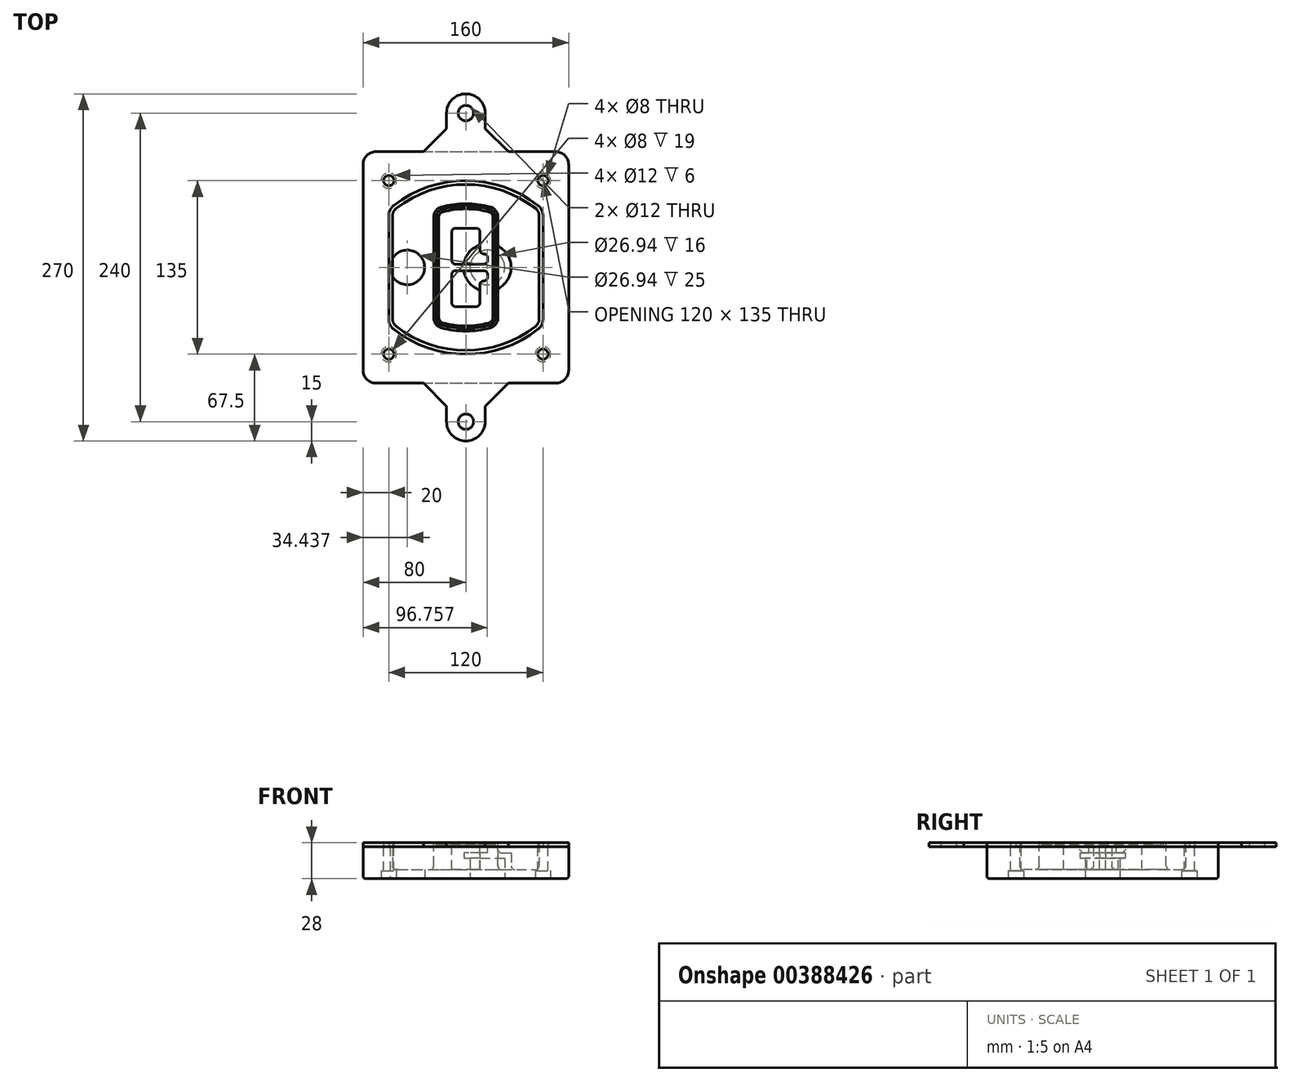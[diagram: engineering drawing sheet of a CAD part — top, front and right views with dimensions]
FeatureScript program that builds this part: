
annotation { "Feature Type Name" : "Feature", "Feature Type Description" : "" }
export const myFeature = defineFeature(function(context is Context, id is Id, definition is map)
    precondition{}
    {
        {
            var Q0;
            Q0=qCreatedBy(makeId("Top.planeOp"),FACE);
            var sketch = newSketch(context, id + "F0", { "sketchPlane" : qUnion([Q0])});
            skPoint(sketch, "E0.rect.middle", {"position": v(0, 0) * mm});
            skLineSegment(sketch, "E1.bottom", {"start": v(-70, -90) * mm, "end": v(70, -90) * mm});
            skLineSegment(sketch, "E1.top", {"start": v(-70, 90) * mm, "end": v(70, 90) * mm});
            skLineSegment(sketch, "E1.left", {"start": v(-80, -80) * mm, "end": v(-80, 80) * mm});
            skLineSegment(sketch, "E1.right", {"start": v(80, -80) * mm, "end": v(80, 80) * mm});
            skLineSegment(sketch, "E2", {"start": v(-80, 90) * mm, "end": v(80, -90) * mm, "construction": true});
            skLineSegment(sketch, "E3", {"start": v(80, 90) * mm, "end": v(-80, -90) * mm, "construction": true});
            skCircle(sketch, "E4", {"center": v(-60, 67.5) * mm, "radius": 4 * mm});
            skCircle(sketch, "E5", {"center": v(60, 67.5) * mm, "radius": 4 * mm});
            skCircle(sketch, "E6", {"center": v(60, -67.5) * mm, "radius": 4 * mm});
            skCircle(sketch, "E7", {"center": v(-60, -67.5) * mm, "radius": 4 * mm});
            skLineSegment(sketch, "E8", {"start": v(-60, 67.5) * mm, "end": v(60, 67.5) * mm, "construction": true});
            skLineSegment(sketch, "E9", {"start": v(60, 67.5) * mm, "end": v(60, -67.5) * mm, "construction": true});
            skLineSegment(sketch, "E10", {"start": v(60, -67.5) * mm, "end": v(-60, -67.5) * mm, "construction": true});
            skLineSegment(sketch, "E11", {"start": v(-60, -67.5) * mm, "end": v(-60, 67.5) * mm, "construction": true});
            skLineSegment(sketch, "E12", {"start": v(-60, 40.3) * mm, "end": v(-60, -40.3) * mm});
            skLineSegment(sketch, "E13", {"start": v(60, 40.3) * mm, "end": v(60, -40.3) * mm});
            skArc(sketch, "E14", {"start": v(56.15, 48.18) * mm, "mid": v(0, 67.5) * mm, "end": v(-56.15, 48.18) * mm});
            skArc(sketch, "E15", {"start": v(-56.15, -48.18) * mm, "mid": v(0, -67.5) * mm, "end": v(56.15, -48.18) * mm});
            skLineSegment(sketch, "E16", {"start": v(-60, 0) * mm, "end": v(60, 0) * mm, "construction": true});
            skPoint(sketch, "E17.visualSharp", {"position": v(-60, -45) * mm});
            skArc(sketch, "E17.filletArc", {"start": v(-60, -40.3) * mm, "mid": v(-58.99, -44.68) * mm, "end": v(-56.15, -48.18) * mm});
            skPoint(sketch, "E18.visualSharp", {"position": v(-60, 45) * mm});
            skArc(sketch, "E18.filletArc", {"start": v(-56.15, 48.18) * mm, "mid": v(-58.99, 44.68) * mm, "end": v(-60, 40.3) * mm});
            skPoint(sketch, "E19.visualSharp", {"position": v(60, 45) * mm});
            skArc(sketch, "E19.filletArc", {"start": v(60, 40.3) * mm, "mid": v(58.99, 44.68) * mm, "end": v(56.15, 48.18) * mm});
            skPoint(sketch, "E20.visualSharp", {"position": v(60, -45) * mm});
            skArc(sketch, "E20.filletArc", {"start": v(56.15, -48.18) * mm, "mid": v(58.99, -44.68) * mm, "end": v(60, -40.3) * mm});
            skPoint(sketch, "E21.visualSharp", {"position": v(-80, 90) * mm});
            skArc(sketch, "E21.filletArc", {"start": v(-70, 90) * mm, "mid": v(-77.07, 87.07) * mm, "end": v(-80, 80) * mm});
            skPoint(sketch, "E22.visualSharp", {"position": v(80, 90) * mm});
            skArc(sketch, "E22.filletArc", {"start": v(80, 80) * mm, "mid": v(77.07, 87.07) * mm, "end": v(70, 90) * mm});
            skPoint(sketch, "E23.visualSharp", {"position": v(80, -90) * mm});
            skArc(sketch, "E23.filletArc", {"start": v(70, -90) * mm, "mid": v(77.07, -87.07) * mm, "end": v(80, -80) * mm});
            skPoint(sketch, "E24.visualSharp", {"position": v(-80, -90) * mm});
            skArc(sketch, "E24.filletArc", {"start": v(-80, -80) * mm, "mid": v(-77.07, -87.07) * mm, "end": v(-70, -90) * mm});
            skArc(sketch, "E25.0", {"start": v(57, 40.3) * mm, "mid": v(56.3, 43.36) * mm, "end": v(54.3, 45.81) * mm});
            skLineSegment(sketch, "E25.1", {"start": v(57, 40.3) * mm, "end": v(57, -40.3) * mm});
            skArc(sketch, "E25.2", {"start": v(54.3, -45.81) * mm, "mid": v(56.3, -43.36) * mm, "end": v(57, -40.3) * mm});
            skArc(sketch, "E25.3", {"start": v(-54.3, -45.81) * mm, "mid": v(0, -64.5) * mm, "end": v(54.3, -45.81) * mm});
            skArc(sketch, "E25.4", {"start": v(-57, -40.3) * mm, "mid": v(-56.3, -43.36) * mm, "end": v(-54.3, -45.81) * mm});
            skArc(sketch, "E25.5", {"start": v(54.3, 45.81) * mm, "mid": v(0, 64.5) * mm, "end": v(-54.3, 45.81) * mm});
            skLineSegment(sketch, "E25.6", {"start": v(-57, 40.3) * mm, "end": v(-57, -40.3) * mm});
            skArc(sketch, "E25.7", {"start": v(-54.3, 45.81) * mm, "mid": v(-56.3, 43.36) * mm, "end": v(-57, 40.3) * mm});
            skArc(sketch, "E26.0", {"start": v(-58.62, 51.33) * mm, "mid": v(-62.58, 46.43) * mm, "end": v(-64, 40.3) * mm});
            skArc(sketch, "E26.1", {"start": v(58.62, 51.33) * mm, "mid": v(0, 71.5) * mm, "end": v(-58.62, 51.33) * mm});
            skArc(sketch, "E26.2", {"start": v(64, 40.3) * mm, "mid": v(62.58, 46.43) * mm, "end": v(58.62, 51.33) * mm});
            skLineSegment(sketch, "E26.3", {"start": v(64, 40.3) * mm, "end": v(64, -40.3) * mm});
            skArc(sketch, "E26.4", {"start": v(58.62, -51.33) * mm, "mid": v(62.58, -46.43) * mm, "end": v(64, -40.3) * mm});
            skLineSegment(sketch, "E26.5", {"start": v(-64, 40.3) * mm, "end": v(-64, -40.3) * mm});
            skArc(sketch, "E26.6", {"start": v(-58.62, -51.33) * mm, "mid": v(0, -71.5) * mm, "end": v(58.62, -51.33) * mm});
            skArc(sketch, "E26.7", {"start": v(-64, -40.3) * mm, "mid": v(-62.58, -46.43) * mm, "end": v(-58.62, -51.33) * mm});
            skSolve(sketch);
        }
        {
            var Q0;
            Q0=makeQuery(id+"F0.imprint","IMPRINT",FACE,{"disambiguationData":[TD([[makeQuery(id+"F0.imprint","IMPRINT",EDGE,{"derivedFrom":sQuery(id+"F0.wireOp",EDGE,"E1.bottom")}),1.0]])]});
            var Q1;
            Q1=makeQuery(id+"F0.imprint","IMPRINT",FACE,{"disambiguationData":[TD([[makeQuery(id+"F0.imprint","IMPRINT",EDGE,{"derivedFrom":sQuery(id+"F0.wireOp",EDGE,"E12")}),1.0]])]});
            var Q2;
            Q2=makeQuery(id+"F0.imprint","IMPRINT",FACE,{"disambiguationData":[TD([[makeQuery(id+"F0.imprint","IMPRINT",EDGE,{"derivedFrom":sQuery(id+"F0.wireOp",EDGE,"E25.0")}),1.0]])]});
            var Q3;
            Q3=makeQuery(id+"F0.imprint","IMPRINT",FACE,{"disambiguationData":[TD([[makeQuery(id+"F0.imprint","IMPRINT",EDGE,{"derivedFrom":sQuery(id+"F0.wireOp",EDGE,"E12")}),-1.0]])]});
            extrude(context, id + "F1", {"entities" : qUnion([Q0, Q1, Q2, Q3]), "oppositeDirection" : true, "depth" : 25 * mm});
        }
        {
            var Q0;
            Q0=makeQuery(id+"F0.imprint","IMPRINT",FACE,{"disambiguationData":[TD([[makeQuery(id+"F0.imprint","IMPRINT",EDGE,{"derivedFrom":sQuery(id+"F0.wireOp",EDGE,"E12")}),1.0]])]});
            extrude(context, id + "F2", {"entities" : qUnion([Q0]), "operationType" : NewBodyOperationType.ADD, "depth" : 3 * mm});
        }
        {
            var Q0;
            Q0=makeQuery(id+"F0.imprint","IMPRINT",FACE,{"disambiguationData":[TD([[makeQuery(id+"F0.imprint","IMPRINT",EDGE,{"derivedFrom":sQuery(id+"F0.wireOp",EDGE,"E25.0")}),1.0]])]});
            extrude(context, id + "F3", {"entities" : qUnion([Q0]), "operationType" : NewBodyOperationType.REMOVE, "oppositeDirection" : true, "depth" : 18 * mm});
        }
        {
            var Q0;
            Q0=makeQuery(id+"F2.opExtrude","CAP_FACE",FACE,{"disambiguationData":[OSD([sQuery(id+"F0.wireOp",EDGE,"E12"),sQuery(id+"F0.wireOp",EDGE,"E13"),sQuery(id+"F0.wireOp",EDGE,"E14"),sQuery(id+"F0.wireOp",EDGE,"E15"),sQuery(id+"F0.wireOp",EDGE,"E17.filletArc"),sQuery(id+"F0.wireOp",EDGE,"E18.filletArc"),sQuery(id+"F0.wireOp",EDGE,"E19.filletArc"),sQuery(id+"F0.wireOp",EDGE,"E20.filletArc"),sQuery(id+"F0.wireOp",EDGE,"E25.0"),sQuery(id+"F0.wireOp",EDGE,"E25.1"),sQuery(id+"F0.wireOp",EDGE,"E25.2"),sQuery(id+"F0.wireOp",EDGE,"E25.3"),sQuery(id+"F0.wireOp",EDGE,"E25.4"),sQuery(id+"F0.wireOp",EDGE,"E25.5"),sQuery(id+"F0.wireOp",EDGE,"E25.6"),sQuery(id+"F0.wireOp",EDGE,"E25.7")])],"isStart":false});
            var sketch = newSketch(context, id + "F4", { "sketchPlane" : qUnion([Q0])});
            skArc(sketch, "E27.0", {"start": v(-19.08, -46.97) * mm, "mid": v(0, -49.5) * mm, "end": v(19.08, -46.97) * mm});
            skArc(sketch, "E28.0", {"start": v(19.08, 46.97) * mm, "mid": v(0, 49.5) * mm, "end": v(-19.08, 46.97) * mm});
            skLineSegment(sketch, "E29", {"start": v(-25, 39.25) * mm, "end": v(-25, -39.25) * mm});
            skLineSegment(sketch, "E30", {"start": v(25, 39.25) * mm, "end": v(25, -39.25) * mm});
            skLineSegment(sketch, "E31", {"start": v(-25, 45.1) * mm, "end": v(25, 45.1) * mm, "construction": true});
            skLineSegment(sketch, "E32", {"start": v(-25, -45.1) * mm, "end": v(25, -45.1) * mm, "construction": true});
            skPoint(sketch, "E33.visualSharp", {"position": v(-25, 45.1) * mm});
            skArc(sketch, "E33.filletArc", {"start": v(-19.08, 46.97) * mm, "mid": v(-23.35, 44.11) * mm, "end": v(-25, 39.25) * mm});
            skPoint(sketch, "E34.visualSharp", {"position": v(25, 45.1) * mm});
            skArc(sketch, "E34.filletArc", {"start": v(25, 39.25) * mm, "mid": v(23.35, 44.11) * mm, "end": v(19.08, 46.97) * mm});
            skPoint(sketch, "E35.visualSharp", {"position": v(25, -45.1) * mm});
            skArc(sketch, "E35.filletArc", {"start": v(19.08, -46.97) * mm, "mid": v(23.35, -44.11) * mm, "end": v(25, -39.25) * mm});
            skPoint(sketch, "E36.visualSharp", {"position": v(-25, -45.1) * mm});
            skArc(sketch, "E36.filletArc", {"start": v(-25, -39.25) * mm, "mid": v(-23.35, -44.11) * mm, "end": v(-19.08, -46.97) * mm});
            skArc(sketch, "E37.0", {"start": v(54.3, 45.81) * mm, "mid": v(0, 64.5) * mm, "end": v(-54.3, 45.81) * mm});
            skArc(sketch, "E37.1", {"start": v(-54.3, 45.81) * mm, "mid": v(-56.3, 43.36) * mm, "end": v(-57, 40.3) * mm});
            skLineSegment(sketch, "E37.2", {"start": v(-57, 40.3) * mm, "end": v(-57, -40.3) * mm});
            skArc(sketch, "E37.3", {"start": v(-57, -40.3) * mm, "mid": v(-56.3, -43.36) * mm, "end": v(-54.3, -45.81) * mm});
            skArc(sketch, "E37.4", {"start": v(-54.3, -45.81) * mm, "mid": v(0, -64.5) * mm, "end": v(54.3, -45.81) * mm});
            skArc(sketch, "E37.5", {"start": v(54.3, -45.81) * mm, "mid": v(56.3, -43.36) * mm, "end": v(57, -40.3) * mm});
            skLineSegment(sketch, "E37.6", {"start": v(57, 40.3) * mm, "end": v(57, -40.3) * mm});
            skArc(sketch, "E37.7", {"start": v(57, 40.3) * mm, "mid": v(56.3, 43.36) * mm, "end": v(54.3, 45.81) * mm});
            skLineSegment(sketch, "E38.0", {"start": v(23, 39.25) * mm, "end": v(23, -39.25) * mm});
            skArc(sketch, "E38.1", {"start": v(18.56, -45.04) * mm, "mid": v(21.76, -42.9) * mm, "end": v(23, -39.25) * mm});
            skArc(sketch, "E38.2", {"start": v(-18.56, -45.04) * mm, "mid": v(0, -47.5) * mm, "end": v(18.56, -45.04) * mm});
            skArc(sketch, "E38.3", {"start": v(-23, -39.25) * mm, "mid": v(-21.76, -42.9) * mm, "end": v(-18.56, -45.04) * mm});
            skLineSegment(sketch, "E38.4", {"start": v(-23, 39.25) * mm, "end": v(-23, -39.25) * mm});
            skArc(sketch, "E38.5", {"start": v(23, 39.25) * mm, "mid": v(21.76, 42.9) * mm, "end": v(18.56, 45.04) * mm});
            skArc(sketch, "E38.6", {"start": v(-18.56, 45.04) * mm, "mid": v(-21.76, 42.9) * mm, "end": v(-23, 39.25) * mm});
            skArc(sketch, "E38.7", {"start": v(18.56, 45.04) * mm, "mid": v(0, 47.5) * mm, "end": v(-18.56, 45.04) * mm});
            skArc(sketch, "E39.0", {"start": v(21, 39.25) * mm, "mid": v(20.18, 41.68) * mm, "end": v(18.04, 43.1) * mm});
            skLineSegment(sketch, "E39.1", {"start": v(21, 39.25) * mm, "end": v(21, -39.25) * mm});
            skArc(sketch, "E39.2", {"start": v(18.04, -43.1) * mm, "mid": v(20.18, -41.68) * mm, "end": v(21, -39.25) * mm});
            skArc(sketch, "E39.3", {"start": v(-18.04, -43.1) * mm, "mid": v(0, -45.5) * mm, "end": v(18.04, -43.1) * mm});
            skArc(sketch, "E39.4", {"start": v(-21, -39.25) * mm, "mid": v(-20.18, -41.68) * mm, "end": v(-18.04, -43.1) * mm});
            skArc(sketch, "E39.5", {"start": v(18.04, 43.1) * mm, "mid": v(0, 45.5) * mm, "end": v(-18.04, 43.1) * mm});
            skLineSegment(sketch, "E39.6", {"start": v(-21, 39.25) * mm, "end": v(-21, -39.25) * mm});
            skArc(sketch, "E39.7", {"start": v(-18.04, 43.1) * mm, "mid": v(-20.18, 41.68) * mm, "end": v(-21, 39.25) * mm});
            skLineSegment(sketch, "E40", {"start": v(-25, 0) * mm, "end": v(25, 0) * mm, "construction": true});
            skLineSegment(sketch, "E41", {"start": v(-11, 5.5) * mm, "end": v(-11, 27.5) * mm});
            skLineSegment(sketch, "E42", {"start": v(-8, 30.5) * mm, "end": v(8, 30.5) * mm});
            skLineSegment(sketch, "E43", {"start": v(11, 27.5) * mm, "end": v(11, 13.5) * mm});
            skLineSegment(sketch, "E44", {"start": v(14, 10.5) * mm, "end": v(14, 10.5) * mm});
            skLineSegment(sketch, "E45", {"start": v(17, 7.5) * mm, "end": v(17, 5.5) * mm});
            skLineSegment(sketch, "E46", {"start": v(14, 2.5) * mm, "end": v(-8, 2.5) * mm});
            skPoint(sketch, "E47.visualSharp", {"position": v(-11, 30.5) * mm});
            skArc(sketch, "E47.filletArc", {"start": v(-8, 30.5) * mm, "mid": v(-10.12, 29.62) * mm, "end": v(-11, 27.5) * mm});
            skPoint(sketch, "E48.visualSharp", {"position": v(11, 30.5) * mm});
            skArc(sketch, "E48.filletArc", {"start": v(11, 27.5) * mm, "mid": v(10.12, 29.62) * mm, "end": v(8, 30.5) * mm});
            skPoint(sketch, "E49.visualSharp", {"position": v(11, 10.5) * mm});
            skArc(sketch, "E49.filletArc", {"start": v(11, 13.5) * mm, "mid": v(11.88, 11.38) * mm, "end": v(14, 10.5) * mm});
            skPoint(sketch, "E50.visualSharp", {"position": v(17, 10.5) * mm});
            skArc(sketch, "E50.filletArc", {"start": v(17, 7.5) * mm, "mid": v(16.12, 9.62) * mm, "end": v(14, 10.5) * mm});
            skPoint(sketch, "E51.visualSharp", {"position": v(17, 2.5) * mm});
            skArc(sketch, "E51.filletArc", {"start": v(14, 2.5) * mm, "mid": v(16.12, 3.38) * mm, "end": v(17, 5.5) * mm});
            skPoint(sketch, "E52.visualSharp", {"position": v(-11, 2.5) * mm});
            skArc(sketch, "E52.filletArc", {"start": v(-11, 5.5) * mm, "mid": v(-10.12, 3.38) * mm, "end": v(-8, 2.5) * mm});
            skLineSegment(sketch, "E53.0.MirrorCS", {"start": v(14, -2.5) * mm, "end": v(-8, -2.5) * mm});
            skArc(sketch, "E54.0.MirrorCS", {"start": v(-11, -5.5) * mm, "mid": v(-10.12, -3.38) * mm, "end": v(-8, -2.5) * mm});
            skLineSegment(sketch, "E55.0.MirrorCS", {"start": v(-11, -5.5) * mm, "end": v(-11, -27.5) * mm});
            skArc(sketch, "E56.0.MirrorCS", {"start": v(-8, -30.5) * mm, "mid": v(-10.12, -29.62) * mm, "end": v(-11, -27.5) * mm});
            skLineSegment(sketch, "E57.0.MirrorCS", {"start": v(-8, -30.5) * mm, "end": v(8, -30.5) * mm});
            skArc(sketch, "E58.0.MirrorCS", {"start": v(11, -27.5) * mm, "mid": v(10.12, -29.62) * mm, "end": v(8, -30.5) * mm});
            skLineSegment(sketch, "E59.0.MirrorCS", {"start": v(11, -27.5) * mm, "end": v(11, -13.5) * mm});
            skArc(sketch, "E60.0.MirrorCS", {"start": v(11, -13.5) * mm, "mid": v(11.88, -11.38) * mm, "end": v(14, -10.5) * mm});
            skArc(sketch, "E61.0.MirrorCS", {"start": v(17, -7.5) * mm, "mid": v(16.12, -9.62) * mm, "end": v(14, -10.5) * mm});
            skLineSegment(sketch, "E62.0.MirrorCS", {"start": v(17, -7.5) * mm, "end": v(17, -5.5) * mm});
            skArc(sketch, "E63.0.MirrorCS", {"start": v(14, -2.5) * mm, "mid": v(16.12, -3.38) * mm, "end": v(17, -5.5) * mm});
            skSolve(sketch);
        }
        {
            var Q0;
            Q0=makeQuery(id+"F4.imprint","IMPRINT",FACE,{"disambiguationData":[TD([[makeQuery(id+"F4.imprint","IMPRINT",EDGE,{"derivedFrom":sQuery(id+"F4.wireOp",EDGE,"E27.0")}),1.0]])]});
            var Q1;
            Q1=makeQuery(id+"F4.imprint","IMPRINT",FACE,{"disambiguationData":[TD([[makeQuery(id+"F4.imprint","IMPRINT",EDGE,{"derivedFrom":sQuery(id+"F4.wireOp",EDGE,"E38.0")}),-1.0]])]});
            var Q2;
            Q2=makeQuery(id+"F4.imprint","IMPRINT",FACE,{"disambiguationData":[TD([[makeQuery(id+"F4.imprint","IMPRINT",EDGE,{"derivedFrom":sQuery(id+"F4.wireOp",EDGE,"E39.0")}),1.0]])]});
            extrude(context, id + "F5", {"entities" : qUnion([Q0, Q1, Q2]), "operationType" : NewBodyOperationType.ADD, "endBound" : BoundingType.UP_TO_NEXT, "oppositeDirection" : true, "depth" : 25 * mm});
        }
        {
            var Q0;
            Q0=makeQuery(id+"F4.imprint","IMPRINT",FACE,{"disambiguationData":[TD([[makeQuery(id+"F4.imprint","IMPRINT",EDGE,{"derivedFrom":sQuery(id+"F4.wireOp",EDGE,"E38.0")}),-1.0]])]});
            extrude(context, id + "F6", {"entities" : qUnion([Q0]), "operationType" : NewBodyOperationType.REMOVE, "oppositeDirection" : true, "depth" : 2 * mm});
        }
        {
            var Q0;
            Q0=makeQuery(id+"F1.opExtrude","CAP_FACE",FACE,{"disambiguationData":[OSD([sQuery(id+"F0.wireOp",EDGE,"E1.bottom"),sQuery(id+"F0.wireOp",EDGE,"E1.top"),sQuery(id+"F0.wireOp",EDGE,"E1.left"),sQuery(id+"F0.wireOp",EDGE,"E1.right"),sQuery(id+"F0.wireOp",EDGE,"E4"),sQuery(id+"F0.wireOp",EDGE,"E5"),sQuery(id+"F0.wireOp",EDGE,"E6"),sQuery(id+"F0.wireOp",EDGE,"E7"),sQuery(id+"F0.wireOp",EDGE,"E21.filletArc"),sQuery(id+"F0.wireOp",EDGE,"E22.filletArc"),sQuery(id+"F0.wireOp",EDGE,"E23.filletArc"),sQuery(id+"F0.wireOp",EDGE,"E24.filletArc")])],"isStart":false});
            var sketch = newSketch(context, id + "F7", { "sketchPlane" : qUnion([Q0])});
            skCircle(sketch, "E64", {"center": v(16.76, 0) * mm, "radius": 13.47 * mm});
            skCircle(sketch, "E65", {"center": v(-45.56, 0) * mm, "radius": 13.47 * mm});
            skLineSegment(sketch, "E66", {"start": v(80, 0) * mm, "end": v(-80, 0) * mm});
            skCircle(sketch, "E67", {"center": v(16.76, 0) * mm, "radius": 18.47 * mm});
            skCircle(sketch, "E68", {"center": v(60, -67.5) * mm, "radius": 6 * mm});
            skCircle(sketch, "E69", {"center": v(-60, -67.5) * mm, "radius": 6 * mm});
            skCircle(sketch, "E70", {"center": v(-60, 67.5) * mm, "radius": 6 * mm});
            skCircle(sketch, "E71", {"center": v(60, 67.5) * mm, "radius": 6 * mm});
            skSolve(sketch);
        }
        {
            var Q0;
            {var subQ1=sQuery(id+"F7.wireOp",EDGE,"E66");var subQ4=sQuery(id+"F7.wireOp",EDGE,"E64");var subQ6=makeQuery(id+"F7.imprint","INTERSECT",VERTEX,{"disambiguationData":[OD(0.0)],"derivedFrom":[subQ4,subQ1]});Q0=makeQuery(id+"F7.imprint","IMPRINT",FACE,{"disambiguationData":[TD([[makeQuery(id+"F7.imprint","IMPRINT",EDGE,{"disambiguationData":[TD([[subQ6,-1.0]])],"derivedFrom":subQ4}),-1.0]])]});}
            var Q1;
            {var subQ0=sQuery(id+"F7.wireOp",EDGE,"E66");var subQ1=sQuery(id+"F7.wireOp",EDGE,"E64");var subQ3=makeQuery(id+"F7.imprint","INTERSECT",VERTEX,{"disambiguationData":[OD(0.0)],"derivedFrom":[subQ1,subQ0]});Q1=makeQuery(id+"F7.imprint","IMPRINT",FACE,{"disambiguationData":[TD([[makeQuery(id+"F7.imprint","IMPRINT",EDGE,{"disambiguationData":[TD([[subQ3,-1.0]])],"derivedFrom":subQ1}),1.0]])]});}
            var Q2;
            {var subQ0=sQuery(id+"F7.wireOp",EDGE,"E66");var subQ1=sQuery(id+"F7.wireOp",EDGE,"E64");var subQ3=makeQuery(id+"F7.imprint","INTERSECT",VERTEX,{"disambiguationData":[OD(0.0)],"derivedFrom":[subQ1,subQ0]});Q2=makeQuery(id+"F7.imprint","IMPRINT",FACE,{"disambiguationData":[TD([[makeQuery(id+"F7.imprint","IMPRINT",EDGE,{"disambiguationData":[TD([[subQ3,1.0]])],"derivedFrom":subQ1}),1.0]])]});}
            var Q3;
            {var subQ1=sQuery(id+"F7.wireOp",EDGE,"E66");var subQ4=sQuery(id+"F7.wireOp",EDGE,"E64");var subQ6=makeQuery(id+"F7.imprint","INTERSECT",VERTEX,{"disambiguationData":[OD(0.0)],"derivedFrom":[subQ4,subQ1]});Q3=makeQuery(id+"F7.imprint","IMPRINT",FACE,{"disambiguationData":[TD([[makeQuery(id+"F7.imprint","IMPRINT",EDGE,{"disambiguationData":[TD([[subQ6,1.0]])],"derivedFrom":subQ4}),-1.0]])]});}
            extrude(context, id + "F8", {"entities" : qUnion([Q0, Q1, Q2, Q3]), "operationType" : NewBodyOperationType.ADD, "oppositeDirection" : true, "depth" : 20 * mm});
        }
        {
            var Q0;
            {var subQ0=sQuery(id+"F7.wireOp",EDGE,"E66");var subQ1=sQuery(id+"F7.wireOp",EDGE,"E64");var subQ3=makeQuery(id+"F7.imprint","INTERSECT",VERTEX,{"disambiguationData":[OD(0.0)],"derivedFrom":[subQ1,subQ0]});Q0=makeQuery(id+"F7.imprint","IMPRINT",FACE,{"disambiguationData":[TD([[makeQuery(id+"F7.imprint","IMPRINT",EDGE,{"disambiguationData":[TD([[subQ3,-1.0]])],"derivedFrom":subQ1}),1.0]])]});}
            var Q1;
            {var subQ0=sQuery(id+"F7.wireOp",EDGE,"E66");var subQ1=sQuery(id+"F7.wireOp",EDGE,"E64");var subQ3=makeQuery(id+"F7.imprint","INTERSECT",VERTEX,{"disambiguationData":[OD(0.0)],"derivedFrom":[subQ1,subQ0]});Q1=makeQuery(id+"F7.imprint","IMPRINT",FACE,{"disambiguationData":[TD([[makeQuery(id+"F7.imprint","IMPRINT",EDGE,{"disambiguationData":[TD([[subQ3,1.0]])],"derivedFrom":subQ1}),1.0]])]});}
            extrude(context, id + "F9", {"entities" : qUnion([Q0, Q1]), "operationType" : NewBodyOperationType.REMOVE, "oppositeDirection" : true, "depth" : 16 * mm});
        }
        {
            var Q0;
            {var subQ0=sQuery(id+"F7.wireOp",EDGE,"E66");var subQ1=sQuery(id+"F7.wireOp",EDGE,"E65");var subQ3=makeQuery(id+"F7.imprint","INTERSECT",VERTEX,{"disambiguationData":[OD(0.0)],"derivedFrom":[subQ1,subQ0]});Q0=makeQuery(id+"F7.imprint","IMPRINT",FACE,{"disambiguationData":[TD([[makeQuery(id+"F7.imprint","IMPRINT",EDGE,{"disambiguationData":[TD([[subQ3,-1.0]])],"derivedFrom":subQ1}),1.0]])]});}
            var Q1;
            {var subQ0=sQuery(id+"F7.wireOp",EDGE,"E66");var subQ1=sQuery(id+"F7.wireOp",EDGE,"E65");var subQ3=makeQuery(id+"F7.imprint","INTERSECT",VERTEX,{"disambiguationData":[OD(0.0)],"derivedFrom":[subQ1,subQ0]});Q1=makeQuery(id+"F7.imprint","IMPRINT",FACE,{"disambiguationData":[TD([[makeQuery(id+"F7.imprint","IMPRINT",EDGE,{"disambiguationData":[TD([[subQ3,1.0]])],"derivedFrom":subQ1}),1.0]])]});}
            extrude(context, id + "F10", {"entities" : qUnion([Q0, Q1]), "operationType" : NewBodyOperationType.REMOVE, "oppositeDirection" : true, "depth" : 25 * mm});
        }
        {
            var Q0;
            Q0=makeQuery(id+"F7.imprint","IMPRINT",FACE,{"disambiguationData":[TD([[makeQuery(id+"F7.imprint","IMPRINT",EDGE,{"derivedFrom":sQuery(id+"F7.wireOp",EDGE,"E68")}),1.0]])]});
            var Q1;
            Q1=makeQuery(id+"F7.imprint","IMPRINT",FACE,{"disambiguationData":[TD([[makeQuery(id+"F7.imprint","IMPRINT",EDGE,{"derivedFrom":makeQuery(id+"F1.opExtrude","CAP_EDGE",EDGE,{"disambiguationData":[OSD([sQuery(id+"F0.wireOp",EDGE,"E5")])],"isStart":false})}),-1.0]])]});
            var Q2;
            Q2=makeQuery(id+"F7.imprint","IMPRINT",FACE,{"disambiguationData":[TD([[makeQuery(id+"F7.imprint","IMPRINT",EDGE,{"derivedFrom":sQuery(id+"F7.wireOp",EDGE,"E69")}),1.0]])]});
            var Q3;
            Q3=makeQuery(id+"F7.imprint","IMPRINT",FACE,{"disambiguationData":[TD([[makeQuery(id+"F7.imprint","IMPRINT",EDGE,{"derivedFrom":makeQuery(id+"F1.opExtrude","CAP_EDGE",EDGE,{"disambiguationData":[OSD([sQuery(id+"F0.wireOp",EDGE,"E4")])],"isStart":false})}),-1.0]])]});
            var Q4;
            Q4=makeQuery(id+"F7.imprint","IMPRINT",FACE,{"disambiguationData":[TD([[makeQuery(id+"F7.imprint","IMPRINT",EDGE,{"derivedFrom":sQuery(id+"F7.wireOp",EDGE,"E70")}),1.0]])]});
            var Q5;
            Q5=makeQuery(id+"F7.imprint","IMPRINT",FACE,{"disambiguationData":[TD([[makeQuery(id+"F7.imprint","IMPRINT",EDGE,{"derivedFrom":makeQuery(id+"F1.opExtrude","CAP_EDGE",EDGE,{"disambiguationData":[OSD([sQuery(id+"F0.wireOp",EDGE,"E7")])],"isStart":false})}),-1.0]])]});
            var Q6;
            Q6=makeQuery(id+"F7.imprint","IMPRINT",FACE,{"disambiguationData":[TD([[makeQuery(id+"F7.imprint","IMPRINT",EDGE,{"derivedFrom":sQuery(id+"F7.wireOp",EDGE,"E71")}),1.0]])]});
            var Q7;
            Q7=makeQuery(id+"F7.imprint","IMPRINT",FACE,{"disambiguationData":[TD([[makeQuery(id+"F7.imprint","IMPRINT",EDGE,{"derivedFrom":makeQuery(id+"F1.opExtrude","CAP_EDGE",EDGE,{"disambiguationData":[OSD([sQuery(id+"F0.wireOp",EDGE,"E6")])],"isStart":false})}),-1.0]])]});
            extrude(context, id + "F11", {"entities" : qUnion([Q0, Q1, Q2, Q3, Q4, Q5, Q6, Q7]), "operationType" : NewBodyOperationType.REMOVE, "oppositeDirection" : true, "depth" : 6 * mm});
        }
        {
            var Q0;
            Q0=makeQuery(id+"F9.boolean.opBoolean","COPY",FACE,{"derivedFrom":makeQuery(id+"F9.opExtrude","CAP_FACE",FACE,{"disambiguationData":[OSD([sQuery(id+"F7.wireOp",EDGE,"E64")])],"isStart":false})});
            var sketch = newSketch(context, id + "F12", { "sketchPlane" : qUnion([Q0])});
            skArc(sketch, "E72.0", {"start": v(11, 17.55) * mm, "mid": v(2.57, 11.82) * mm, "end": v(-1.54, 2.5) * mm});
            skArc(sketch, "E72.1", {"start": v(-1.54, -2.5) * mm, "mid": v(2.57, -11.82) * mm, "end": v(11, -17.55) * mm});
            skLineSegment(sketch, "E73", {"start": v(-1.54, -2.5) * mm, "end": v(14, -2.5) * mm});
            skLineSegment(sketch, "E74.0", {"start": v(14, 2.5) * mm, "end": v(-1.54, 2.5) * mm});
            skArc(sketch, "E74.1", {"start": v(14, 2.5) * mm, "mid": v(16.12, 3.38) * mm, "end": v(17, 5.5) * mm});
            skLineSegment(sketch, "E74.2", {"start": v(17, 7.5) * mm, "end": v(17, 5.5) * mm});
            skArc(sketch, "E74.3", {"start": v(17, 7.5) * mm, "mid": v(16.12, 9.62) * mm, "end": v(14, 10.5) * mm});
            skArc(sketch, "E74.4", {"start": v(11, 13.5) * mm, "mid": v(11.88, 11.38) * mm, "end": v(14, 10.5) * mm});
            skLineSegment(sketch, "E74.5", {"start": v(11, 17.55) * mm, "end": v(11, 13.5) * mm});
            skLineSegment(sketch, "E74.7", {"start": v(14, -2.5) * mm, "end": v(-1.54, -2.5) * mm});
            skArc(sketch, "E74.8", {"start": v(14, -2.5) * mm, "mid": v(16.12, -3.38) * mm, "end": v(17, -5.5) * mm});
            skLineSegment(sketch, "E74.9", {"start": v(17, -7.5) * mm, "end": v(17, -5.5) * mm});
            skArc(sketch, "E74.10", {"start": v(17, -7.5) * mm, "mid": v(16.12, -9.62) * mm, "end": v(14, -10.5) * mm});
            skArc(sketch, "E74.11", {"start": v(11, -13.5) * mm, "mid": v(11.88, -11.38) * mm, "end": v(14, -10.5) * mm});
            skLineSegment(sketch, "E74.12", {"start": v(11, -17.55) * mm, "end": v(11, -13.5) * mm});
            skPoint(sketch, "E75.orphan", {"position": v(11, -27.5) * mm});
            skPoint(sketch, "E76.orphan", {"position": v(-8, -2.5) * mm});
            skPoint(sketch, "E77.orphan", {"position": v(-8, 2.5) * mm});
            skPoint(sketch, "E78.orphan", {"position": v(11, 27.5) * mm});
            skSolve(sketch);
        }
        {
            var Q0;
            {var subQ7=sQuery(id+"F12.wireOp",EDGE,"E72.0");var subQ14=sQuery(id+"F12.wireOp",EDGE,"E72.1");var subQ16=sQuery(id+"F12.wireOp",EDGE,"E74.1");var subQ18=sQuery(id+"F12.wireOp",EDGE,"E74.8");Q0=qUnion([makeQuery(id+"F12.imprint","IMPRINT",FACE,{"disambiguationData":[TD([[makeQuery(id+"F12.imprint","IMPRINT",EDGE,{"derivedFrom":subQ7}),1.0]])]}),makeQuery(id+"F12.imprint","IMPRINT",FACE,{"disambiguationData":[TD([[makeQuery(id+"F12.imprint","IMPRINT",EDGE,{"derivedFrom":subQ14}),1.0]])]}),makeQuery(id+"F12.imprint","IMPRINT",FACE,{"disambiguationData":[TD([[makeQuery(id+"F12.imprint","IMPRINT",EDGE,{"derivedFrom":subQ16}),1.0]])]}),makeQuery(id+"F12.imprint","IMPRINT",FACE,{"disambiguationData":[TD([[makeQuery(id+"F12.imprint","IMPRINT",EDGE,{"derivedFrom":subQ18}),-1.0]])]})]);}
            var Q1;
            Q1=makeQuery(id+"F5.boolean.opBoolean","SPLIT",FACE,{"disambiguationData":[TD([makeQuery(id+"F5.opExtrude","SWEPT_FACE",FACE,{"disambiguationData":[OSD([sQuery(id+"F4.wireOp",EDGE,"E41")])]})])],"derivedFrom":makeQuery(id+"F3.boolean.opBoolean","COPY",FACE,{"derivedFrom":makeQuery(id+"F3.opExtrude","CAP_FACE",FACE,{"disambiguationData":[OSD([sQuery(id+"F0.wireOp",EDGE,"E25.0"),sQuery(id+"F0.wireOp",EDGE,"E25.1"),sQuery(id+"F0.wireOp",EDGE,"E25.2"),sQuery(id+"F0.wireOp",EDGE,"E25.3"),sQuery(id+"F0.wireOp",EDGE,"E25.4"),sQuery(id+"F0.wireOp",EDGE,"E25.5"),sQuery(id+"F0.wireOp",EDGE,"E25.6"),sQuery(id+"F0.wireOp",EDGE,"E25.7")])],"isStart":false})})});
            extrude(context, id + "F13", {"entities" : qUnion([Q0]), "operationType" : NewBodyOperationType.REMOVE, "endBound" : BoundingType.UP_TO_SURFACE, "endBoundEntityFace" : qUnion([Q1]), "depth" : 25 * mm});
        }
        {
            var Q0;
            Q0=makeQuery(id+"F3.boolean.opBoolean","COPY",EDGE,{"derivedFrom":makeQuery(id+"F3.opExtrude","CAP_EDGE",EDGE,{"disambiguationData":[OSD([sQuery(id+"F0.wireOp",EDGE,"E25.6")])],"isStart":false})});
            var Q1;
            Q1=makeQuery(id+"F8.boolean.opBoolean","INTERSECT",EDGE,{"derivedFrom":[makeQuery(id+"F5.opExtrude","SWEPT_FACE",FACE,{"disambiguationData":[OSD([sQuery(id+"F4.wireOp",EDGE,"E30")])]}),makeQuery(id+"F8.opExtrude","CAP_FACE",FACE,{"disambiguationData":[OSD([sQuery(id+"F7.wireOp",EDGE,"E67")])],"isStart":false})]});
            var Q2;
            Q2=makeQuery(id+"F8.boolean.opBoolean","INTERSECT",EDGE,{"disambiguationData":[OD(1.0)],"derivedFrom":[makeQuery(id+"F5.opExtrude","SWEPT_FACE",FACE,{"disambiguationData":[OSD([sQuery(id+"F4.wireOp",EDGE,"E30")])]}),makeQuery(id+"F8.opExtrude","SWEPT_FACE",FACE,{"disambiguationData":[OSD([sQuery(id+"F7.wireOp",EDGE,"E67")])]})]});
            var Q3;
            {var subQ0=sQuery(id+"F4.wireOp",EDGE,"E30");Q3=makeQuery(id+"F8.boolean.opBoolean","SPLIT",EDGE,{"disambiguationData":[TD([makeQuery(id+"F5.opExtrude","SWEPT_FACE",FACE,{"disambiguationData":[OSD([sQuery(id+"F4.wireOp",EDGE,"E35.filletArc")])]})])],"derivedFrom":makeQuery(id+"F5.opExtrude","CAP_EDGE",EDGE,{"disambiguationData":[OSD([subQ0])],"isStart":false})});}
            var Q4;
            {var subQ0=sQuery(id+"F0.wireOp",EDGE,"E25.7");var subQ1=sQuery(id+"F0.wireOp",EDGE,"E25.1");var subQ2=sQuery(id+"F0.wireOp",EDGE,"E25.6");var subQ3=sQuery(id+"F0.wireOp",EDGE,"E25.5");var subQ4=sQuery(id+"F0.wireOp",EDGE,"E25.4");var subQ5=sQuery(id+"F0.wireOp",EDGE,"E25.0");var subQ6=sQuery(id+"F0.wireOp",EDGE,"E25.2");var subQ7=sQuery(id+"F0.wireOp",EDGE,"E25.3");Q4=makeQuery(id+"F8.boolean.opBoolean","INTERSECT",EDGE,{"derivedFrom":[makeQuery(id+"F5.boolean.opBoolean","SPLIT",FACE,{"disambiguationData":[TD([makeQuery(id+"F2.opExtrude","SWEPT_FACE",FACE,{"disambiguationData":[OSD([subQ5])]})])],"derivedFrom":makeQuery(id+"F3.boolean.opBoolean","COPY",FACE,{"derivedFrom":makeQuery(id+"F3.opExtrude","CAP_FACE",FACE,{"disambiguationData":[OSD([subQ5,subQ1,subQ6,subQ7,subQ4,subQ3,subQ2,subQ0])],"isStart":false})})}),makeQuery(id+"F8.opExtrude","SWEPT_FACE",FACE,{"disambiguationData":[OSD([sQuery(id+"F7.wireOp",EDGE,"E67")])]})]});}
            var Q5;
            Q5=makeQuery(id+"F8.boolean.opBoolean","INTERSECT",EDGE,{"disambiguationData":[OD(0.0)],"derivedFrom":[makeQuery(id+"F5.opExtrude","SWEPT_FACE",FACE,{"disambiguationData":[OSD([sQuery(id+"F4.wireOp",EDGE,"E30")])]}),makeQuery(id+"F8.opExtrude","SWEPT_FACE",FACE,{"disambiguationData":[OSD([sQuery(id+"F7.wireOp",EDGE,"E67")])]})]});
            fillet(context, id + "F14", {"entities" : qUnion([Q0, Q1, Q2, Q3, Q4, Q5]), "radius" : 3 * mm, "tangentPropagation" : true, "allowEdgeOverflow" : false});
        }
        {
            var Q0;
            Q0=makeQuery(id+"F1.opExtrude","CAP_EDGE",EDGE,{"disambiguationData":[OSD([sQuery(id+"F0.wireOp",EDGE,"E1.bottom")])],"isStart":false});
            fillet(context, id + "F15", {"entities" : qUnion([Q0]), "radius" : 2 * mm, "tangentPropagation" : true, "allowEdgeOverflow" : false});
        }
        {
            var Q0;
            {var subQ0=sQuery(id+"F0.wireOp",EDGE,"E21.filletArc");var subQ1=sQuery(id+"F0.wireOp",EDGE,"E7");var subQ2=sQuery(id+"F0.wireOp",EDGE,"E6");var subQ3=sQuery(id+"F0.wireOp",EDGE,"E5");var subQ4=sQuery(id+"F0.wireOp",EDGE,"E4");var subQ5=sQuery(id+"F0.wireOp",EDGE,"E22.filletArc");var subQ6=sQuery(id+"F0.wireOp",EDGE,"E1.bottom");var subQ7=sQuery(id+"F0.wireOp",EDGE,"E1.right");var subQ8=sQuery(id+"F0.wireOp",EDGE,"E1.top");var subQ9=sQuery(id+"F0.wireOp",EDGE,"E1.left");var subQ10=sQuery(id+"F0.wireOp",EDGE,"E23.filletArc");var subQ11=sQuery(id+"F0.wireOp",EDGE,"E24.filletArc");Q0=makeQuery(id+"F2.boolean.opBoolean","SPLIT",FACE,{"disambiguationData":[TD([makeQuery(id+"F1.opExtrude","SWEPT_FACE",FACE,{"disambiguationData":[OSD([subQ6])]})])],"derivedFrom":makeQuery(id+"F1.opExtrude","CAP_FACE",FACE,{"disambiguationData":[OSD([subQ6,subQ8,subQ9,subQ7,subQ4,subQ3,subQ2,subQ1,subQ0,subQ5,subQ10,subQ11])],"isStart":true})});}
            var sketch = newSketch(context, id + "F16", { "sketchPlane" : qUnion([Q0])});
            skLineSegment(sketch, "E79", {"start": v(0, 90) * mm, "end": v(0, 120) * mm, "construction": true});
            skCircle(sketch, "E80", {"center": v(0, 120) * mm, "radius": 6 * mm});
            skLineSegment(sketch, "E81", {"start": v(-33, 90) * mm, "end": v(-15, 108) * mm});
            skLineSegment(sketch, "E82", {"start": v(-15, 108) * mm, "end": v(-15, 120) * mm});
            skLineSegment(sketch, "E83.MirrorCS", {"start": v(15, 108) * mm, "end": v(15, 120) * mm});
            skLineSegment(sketch, "E84.MirrorCS", {"start": v(33, 90) * mm, "end": v(15, 108) * mm});
            skArc(sketch, "E85", {"start": v(15, 120) * mm, "mid": v(0, 135) * mm, "end": v(-15, 120) * mm});
            skLineSegment(sketch, "E86", {"start": v(-80, 0) * mm, "end": v(80, 0) * mm, "construction": true});
            skArc(sketch, "E87.MirrorCS", {"start": v(-15, 120) * mm, "mid": v(0, 135) * mm, "end": v(15, 120) * mm});
            skArc(sketch, "E88.MirrorCS", {"start": v(15, -120) * mm, "mid": v(0, -135) * mm, "end": v(-15, -120) * mm});
            skLineSegment(sketch, "E89.MirrorCS", {"start": v(15, -108) * mm, "end": v(15, -120) * mm});
            skLineSegment(sketch, "E90.MirrorCS", {"start": v(33, -90) * mm, "end": v(15, -108) * mm});
            skLineSegment(sketch, "E91.MirrorCS", {"start": v(-15, -108) * mm, "end": v(-15, -120) * mm});
            skLineSegment(sketch, "E92.MirrorCS", {"start": v(-33, -90) * mm, "end": v(-15, -108) * mm});
            skCircle(sketch, "E93.MirrorC", {"center": v(0, -120) * mm, "radius": 6 * mm});
            skArc(sketch, "E94.MirrorCS", {"start": v(-15, -120) * mm, "mid": v(0, -135) * mm, "end": v(15, -120) * mm});
            skLineSegment(sketch, "E95.MirrorCS", {"start": v(0, -90) * mm, "end": v(0, -120) * mm, "construction": true});
            skLineSegment(sketch, "E96", {"start": v(-33, 90) * mm, "end": v(33, 90) * mm});
            skLineSegment(sketch, "E97", {"start": v(-33, -90) * mm, "end": v(33, -90) * mm});
            skPoint(sketch, "E98.0", {"position": v(60, -40.3) * mm});
            skArc(sketch, "E98.1", {"start": v(-56.15, -48.18) * mm, "mid": v(0, -67.5) * mm, "end": v(56.15, -48.18) * mm});
            skArc(sketch, "E98.2", {"start": v(-56.15, 48.18) * mm, "mid": v(-58.99, 44.68) * mm, "end": v(-60, 40.3) * mm});
            skArc(sketch, "E98.3", {"start": v(70, -90) * mm, "mid": v(77.07, -87.07) * mm, "end": v(80, -80) * mm});
            skArc(sketch, "E98.4", {"start": v(-70, 90) * mm, "mid": v(-77.07, 87.07) * mm, "end": v(-80, 80) * mm});
            skArc(sketch, "E98.5", {"start": v(56.15, 48.18) * mm, "mid": v(0, 67.5) * mm, "end": v(-56.15, 48.18) * mm});
            skLineSegment(sketch, "E98.6", {"start": v(-80, -80) * mm, "end": v(-80, 80) * mm});
            skLineSegment(sketch, "E98.7", {"start": v(-60, 40.3) * mm, "end": v(-60, -40.3) * mm});
            skCircle(sketch, "E98.8", {"center": v(-60, -67.5) * mm, "radius": 4 * mm});
            skCircle(sketch, "E98.9", {"center": v(60, 67.5) * mm, "radius": 4 * mm});
            skPoint(sketch, "E98.10", {"position": v(80, 80) * mm});
            skArc(sketch, "E98.11", {"start": v(60, 40.3) * mm, "mid": v(58.99, 44.68) * mm, "end": v(56.15, 48.18) * mm});
            skLineSegment(sketch, "E98.12", {"start": v(-70, 90) * mm, "end": v(70, 90) * mm});
            skArc(sketch, "E98.13", {"start": v(-80, -80) * mm, "mid": v(-77.07, -87.07) * mm, "end": v(-70, -90) * mm});
            skLineSegment(sketch, "E98.14", {"start": v(80, -80) * mm, "end": v(80, 80) * mm});
            skArc(sketch, "E98.15", {"start": v(-60, -40.3) * mm, "mid": v(-58.99, -44.68) * mm, "end": v(-56.15, -48.18) * mm});
            skArc(sketch, "E98.16", {"start": v(80, 80) * mm, "mid": v(77.07, 87.07) * mm, "end": v(70, 90) * mm});
            skLineSegment(sketch, "E98.17", {"start": v(60, 40.3) * mm, "end": v(60, -40.3) * mm});
            skLineSegment(sketch, "E98.18", {"start": v(-70, -90) * mm, "end": v(70, -90) * mm});
            skCircle(sketch, "E98.19", {"center": v(60, -67.5) * mm, "radius": 4 * mm});
            skCircle(sketch, "E98.20", {"center": v(-60, 67.5) * mm, "radius": 4 * mm});
            skArc(sketch, "E98.21", {"start": v(56.15, -48.18) * mm, "mid": v(58.99, -44.68) * mm, "end": v(60, -40.3) * mm});
            skSolve(sketch);
        }
        {
            var Q0;
            Q0 = qSketchRegion(id + "F16", true);
            var Q1;
            Q1=makeQuery(id+"F2.opExtrude","CAP_FACE",FACE,{"disambiguationData":[OSD([sQuery(id+"F0.wireOp",EDGE,"E12"),sQuery(id+"F0.wireOp",EDGE,"E13"),sQuery(id+"F0.wireOp",EDGE,"E14"),sQuery(id+"F0.wireOp",EDGE,"E15"),sQuery(id+"F0.wireOp",EDGE,"E17.filletArc"),sQuery(id+"F0.wireOp",EDGE,"E18.filletArc"),sQuery(id+"F0.wireOp",EDGE,"E19.filletArc"),sQuery(id+"F0.wireOp",EDGE,"E20.filletArc"),sQuery(id+"F0.wireOp",EDGE,"E25.0"),sQuery(id+"F0.wireOp",EDGE,"E25.1"),sQuery(id+"F0.wireOp",EDGE,"E25.2"),sQuery(id+"F0.wireOp",EDGE,"E25.3"),sQuery(id+"F0.wireOp",EDGE,"E25.4"),sQuery(id+"F0.wireOp",EDGE,"E25.5"),sQuery(id+"F0.wireOp",EDGE,"E25.6"),sQuery(id+"F0.wireOp",EDGE,"E25.7")])],"isStart":false});
            extrude(context, id + "F17", {"entities" : qUnion([Q0]), "endBound" : BoundingType.UP_TO_SURFACE, "endBoundEntityFace" : qUnion([Q1]), "depth" : 25 * mm});
        }
    });
